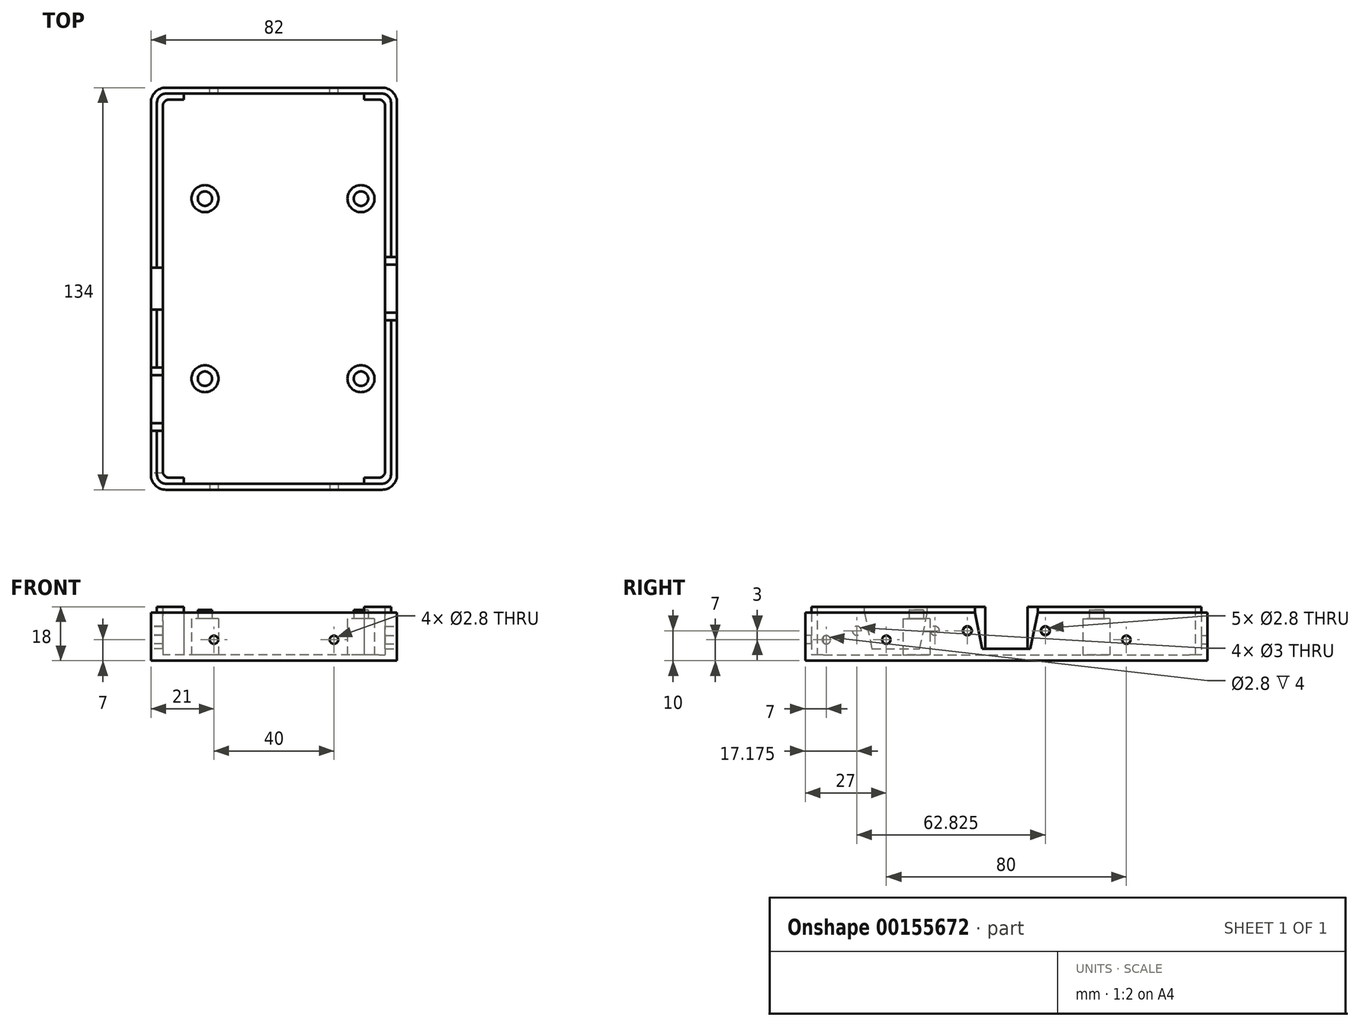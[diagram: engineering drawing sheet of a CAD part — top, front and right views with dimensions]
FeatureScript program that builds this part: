
annotation { "Feature Type Name" : "Feature", "Feature Type Description" : "" }
export const myFeature = defineFeature(function(context is Context, id is Id, definition is map)
    precondition{}
    {
        {
            var Q0;
            Q0=qCreatedBy(makeId("Top.planeOp"),FACE);
            var sketch = newSketch(context, id + "F0", { "sketchPlane" : qUnion([Q0])});
            skLineSegment(sketch, "E0.bottom", {"start": v(36, -67) * mm, "end": v(-36, -67) * mm});
            skLineSegment(sketch, "E0.top", {"start": v(36, 67) * mm, "end": v(-36, 67) * mm});
            skLineSegment(sketch, "E0.left", {"start": v(41, -62) * mm, "end": v(41, 62) * mm});
            skLineSegment(sketch, "E0.right", {"start": v(-41, -62) * mm, "end": v(-41, 62) * mm});
            skPoint(sketch, "E0.middle", {"position": v(0, 0) * mm});
            skPoint(sketch, "E1.visualSharp", {"position": v(-41, 67) * mm});
            skArc(sketch, "E1.filletArc", {"start": v(-36, 67) * mm, "mid": v(-39.54, 65.54) * mm, "end": v(-41, 62) * mm});
            skPoint(sketch, "E2.visualSharp", {"position": v(41, 67) * mm});
            skArc(sketch, "E2.filletArc", {"start": v(41, 62) * mm, "mid": v(39.54, 65.54) * mm, "end": v(36, 67) * mm});
            skPoint(sketch, "E3.visualSharp", {"position": v(41, -67) * mm});
            skArc(sketch, "E3.filletArc", {"start": v(36, -67) * mm, "mid": v(39.54, -65.54) * mm, "end": v(41, -62) * mm});
            skPoint(sketch, "E4.visualSharp", {"position": v(-41, -67) * mm});
            skArc(sketch, "E4.filletArc", {"start": v(-41, -62) * mm, "mid": v(-39.54, -65.54) * mm, "end": v(-36, -67) * mm});
            skSolve(sketch);
        }
        {
            var Q0;
            Q0=qSketchRegion(id+"F0",true);
            extrude(context, id + "F1", {"entities" : qUnion([Q0]), "depth" : 16 * mm});
        }
        {
            var Q0;
            Q0=makeQuery(id+"F1.opExtrude","CAP_FACE",FACE,{"disambiguationData":[OSD([sQuery(id+"F0.wireOp",EDGE,"E0.bottom"),sQuery(id+"F0.wireOp",EDGE,"E0.top"),sQuery(id+"F0.wireOp",EDGE,"E0.left"),sQuery(id+"F0.wireOp",EDGE,"E0.right"),sQuery(id+"F0.wireOp",EDGE,"E1.filletArc"),sQuery(id+"F0.wireOp",EDGE,"E2.filletArc"),sQuery(id+"F0.wireOp",EDGE,"E3.filletArc"),sQuery(id+"F0.wireOp",EDGE,"E4.filletArc")])],"isStart":false});
            shell(context, id + "F2", {"entities" : qUnion([Q0]), "thickness" : 2 * mm});
        }
        {
            var Q0;
            Q0=makeQuery(id+"F2.opShell","OFFSET_FACE",FACE,{"disambiguationData":[OSD([sQuery(id+"F0.wireOp",EDGE,"E0.bottom"),sQuery(id+"F0.wireOp",EDGE,"E0.top"),sQuery(id+"F0.wireOp",EDGE,"E0.left"),sQuery(id+"F0.wireOp",EDGE,"E0.right"),sQuery(id+"F0.wireOp",EDGE,"E1.filletArc"),sQuery(id+"F0.wireOp",EDGE,"E2.filletArc"),sQuery(id+"F0.wireOp",EDGE,"E3.filletArc"),sQuery(id+"F0.wireOp",EDGE,"E4.filletArc")])]});
            var sketch = newSketch(context, id + "F3", { "sketchPlane" : qUnion([Q0])});
            skCircle(sketch, "E5", {"center": v(-23, 30) * mm, "radius": 4.5 * mm});
            skCircle(sketch, "E6", {"center": v(29, 30) * mm, "radius": 4.5 * mm});
            skCircle(sketch, "E7", {"center": v(-23, -30) * mm, "radius": 4.5 * mm});
            skCircle(sketch, "E8", {"center": v(29, -30) * mm, "radius": 4.5 * mm});
            skLineSegment(sketch, "E9.bottom", {"start": v(36, -65) * mm, "end": v(30, -65) * mm});
            skLineSegment(sketch, "E9.top", {"start": v(36, 65) * mm, "end": v(30, 65) * mm});
            skLineSegment(sketch, "E9.left", {"start": v(39, -62) * mm, "end": v(39, 62) * mm});
            skLineSegment(sketch, "E9.right", {"start": v(-39, -62) * mm, "end": v(-39, 62) * mm});
            skPoint(sketch, "E9.middle", {"position": v(0, 0) * mm});
            skLineSegment(sketch, "E10.bottom", {"start": v(35, -63) * mm, "end": v(30, -63) * mm});
            skLineSegment(sketch, "E10.top", {"start": v(35, 63) * mm, "end": v(30, 63) * mm});
            skLineSegment(sketch, "E10.left", {"start": v(37, -61) * mm, "end": v(37, 61) * mm});
            skLineSegment(sketch, "E10.right", {"start": v(-37, -61) * mm, "end": v(-37, 61) * mm});
            skPoint(sketch, "E11.visualSharp", {"position": v(-39, -65) * mm});
            skArc(sketch, "E11.filletArc", {"start": v(-39, -62) * mm, "mid": v(-38.12, -64.12) * mm, "end": v(-36, -65) * mm});
            skPoint(sketch, "E12.visualSharp", {"position": v(39, -65) * mm});
            skArc(sketch, "E12.filletArc", {"start": v(36, -65) * mm, "mid": v(38.12, -64.12) * mm, "end": v(39, -62) * mm});
            skPoint(sketch, "E13.visualSharp", {"position": v(-39, 65) * mm});
            skArc(sketch, "E13.filletArc", {"start": v(-36, 65) * mm, "mid": v(-38.12, 64.12) * mm, "end": v(-39, 62) * mm});
            skPoint(sketch, "E14.visualSharp", {"position": v(39, 65) * mm});
            skArc(sketch, "E14.filletArc", {"start": v(39, 62) * mm, "mid": v(38.12, 64.12) * mm, "end": v(36, 65) * mm});
            skPoint(sketch, "E15.visualSharp", {"position": v(-37, 63) * mm});
            skArc(sketch, "E15.filletArc", {"start": v(-35, 63) * mm, "mid": v(-36.41, 62.41) * mm, "end": v(-37, 61) * mm});
            skPoint(sketch, "E16.visualSharp", {"position": v(37, 63) * mm});
            skArc(sketch, "E16.filletArc", {"start": v(37, 61) * mm, "mid": v(36.41, 62.41) * mm, "end": v(35, 63) * mm});
            skPoint(sketch, "E17.visualSharp", {"position": v(-37, -63) * mm});
            skArc(sketch, "E17.filletArc", {"start": v(-37, -61) * mm, "mid": v(-36.41, -62.41) * mm, "end": v(-35, -63) * mm});
            skPoint(sketch, "E18.visualSharp", {"position": v(37, -63) * mm});
            skArc(sketch, "E18.filletArc", {"start": v(35, -63) * mm, "mid": v(36.41, -62.41) * mm, "end": v(37, -61) * mm});
            skLineSegment(sketch, "E19", {"start": v(-30, 65) * mm, "end": v(-30, 63) * mm});
            skLineSegment(sketch, "E20", {"start": v(30, 65) * mm, "end": v(30, 63) * mm});
            skLineSegment(sketch, "E21.trimOffspring", {"start": v(-30, 65) * mm, "end": v(-36, 65) * mm});
            skLineSegment(sketch, "E22.trimOffspring", {"start": v(-30, 63) * mm, "end": v(-35, 63) * mm});
            skLineSegment(sketch, "E23.trimOffspring", {"start": v(-30, -63) * mm, "end": v(-35, -63) * mm});
            skLineSegment(sketch, "E24.trimOffspring", {"start": v(-30, -65) * mm, "end": v(-36, -65) * mm});
            skLineSegment(sketch, "E25.trimOffspring", {"start": v(30, -63) * mm, "end": v(30, -65) * mm});
            skLineSegment(sketch, "E26.trimOffspring", {"start": v(-30, -63) * mm, "end": v(-30, -65) * mm});
            skSolve(sketch);
        }
        {
            var Q0;
            Q0=makeQuery(id+"F3.imprint","IMPRINT",FACE,{"disambiguationData":[TD([[makeQuery(id+"F3.imprint","IMPRINT",EDGE,{"derivedFrom":sQuery(id+"F3.wireOp",EDGE,"E5")}),1.0]])]});
            var Q1;
            Q1=makeQuery(id+"F3.imprint","IMPRINT",FACE,{"disambiguationData":[TD([[makeQuery(id+"F3.imprint","IMPRINT",EDGE,{"derivedFrom":sQuery(id+"F3.wireOp",EDGE,"E7")}),1.0]])]});
            var Q2;
            Q2=makeQuery(id+"F3.imprint","IMPRINT",FACE,{"disambiguationData":[TD([[makeQuery(id+"F3.imprint","IMPRINT",EDGE,{"derivedFrom":sQuery(id+"F3.wireOp",EDGE,"E8")}),1.0]])]});
            var Q3;
            Q3=makeQuery(id+"F3.imprint","IMPRINT",FACE,{"disambiguationData":[TD([[makeQuery(id+"F3.imprint","IMPRINT",EDGE,{"derivedFrom":sQuery(id+"F3.wireOp",EDGE,"E6")}),1.0]])]});
            extrude(context, id + "F4", {"entities" : qUnion([Q0, Q1, Q2, Q3]), "operationType" : NewBodyOperationType.ADD, "depth" : 12 * mm});
        }
        {
            var Q0;
            Q0=makeQuery(id+"F4.opExtrude","CAP_FACE",FACE,{"disambiguationData":[OSD([sQuery(id+"F3.wireOp",EDGE,"E5")])],"isStart":false});
            var Q1;
            Q1=makeQuery(id+"F4.opExtrude","CAP_FACE",FACE,{"disambiguationData":[OSD([sQuery(id+"F3.wireOp",EDGE,"E6")])],"isStart":false});
            cPlane(context, id + "F5", {"entities" : qUnion([Q0, Q1]), "cplaneType" : CPlaneType.MID_PLANE, "offset" : 25 * mm, "width" : 150 * mm, "height" : 150 * mm});
        }
        {
            var Q0;
            Q0=qCreatedBy(id+"F5.planeOp",FACE);
            var sketch = newSketch(context, id + "F6", { "sketchPlane" : qUnion([Q0])});
            skCircle(sketch, "E27", {"center": v(-23, 30) * mm, "radius": 2.4 * mm});
            skCircle(sketch, "E28", {"center": v(29, 30) * mm, "radius": 2.4 * mm});
            skCircle(sketch, "E29", {"center": v(-23, -30) * mm, "radius": 2.4 * mm});
            skCircle(sketch, "E30", {"center": v(29, -30) * mm, "radius": 2.4 * mm});
            skSolve(sketch);
        }
        {
            var Q0;
            Q0=qSketchRegion(id+"F6",true);
            extrude(context, id + "F7", {"entities" : qUnion([Q0]), "operationType" : NewBodyOperationType.ADD, "depth" : 3 * mm});
        }
        {
            var Q0;
            Q0=makeQuery(id+"F3.imprint","IMPRINT",FACE,{"disambiguationData":[TD([[makeQuery(id+"F3.imprint","IMPRINT",EDGE,{"derivedFrom":sQuery(id+"F3.wireOp",EDGE,"E9.bottom")}),-1.0]])]});
            var Q1;
            Q1=makeQuery(id+"F3.imprint","IMPRINT",FACE,{"disambiguationData":[TD([[makeQuery(id+"F3.imprint","IMPRINT",EDGE,{"derivedFrom":sQuery(id+"F3.wireOp",EDGE,"E9.right")}),-1.0]])]});
            extrude(context, id + "F8", {"entities" : qUnion([Q0, Q1]), "operationType" : NewBodyOperationType.ADD, "depth" : 16 * mm});
        }
        {
            var Q0;
            Q0=makeQuery(id+"F1.opExtrude","SWEPT_FACE",FACE,{"disambiguationData":[OSD([sQuery(id+"F0.wireOp",EDGE,"E0.right")])]});
            var sketch = newSketch(context, id + "F9", { "sketchPlane" : qUnion([Q0])});
            skCircle(sketch, "E31", {"center": v(-13, 10) * mm, "radius": 1.4 * mm});
            skCircle(sketch, "E32", {"center": v(13, 10) * mm, "radius": 1.4 * mm});
            skLineSegment(sketch, "E33.bottom", {"start": v(7, 4) * mm, "end": v(-7, 4) * mm});
            skLineSegment(sketch, "E33.top", {"start": v(7, 16) * mm, "end": v(-7, 16) * mm});
            skLineSegment(sketch, "E33.left", {"start": v(7, 4) * mm, "end": v(7, 16) * mm});
            skLineSegment(sketch, "E33.right", {"start": v(-7, 4) * mm, "end": v(-7, 16) * mm});
            skPoint(sketch, "E33.middle", {"position": v(0, 10) * mm});
            skCircle(sketch, "E34", {"center": v(23.83, 10) * mm, "radius": 1.5 * mm});
            skCircle(sketch, "E35", {"center": v(49.83, 10) * mm, "radius": 1.5 * mm});
            skLineSegment(sketch, "E36", {"start": v(26.33, 16) * mm, "end": v(47.33, 16) * mm});
            skLineSegment(sketch, "E37", {"start": v(47.33, 16) * mm, "end": v(44.83, 4) * mm});
            skLineSegment(sketch, "E38", {"start": v(44.83, 4) * mm, "end": v(28.83, 4) * mm});
            skLineSegment(sketch, "E39", {"start": v(28.83, 4) * mm, "end": v(26.33, 16) * mm});
            skLineSegment(sketch, "E40.bottom", {"start": v(-7, 16) * mm, "end": v(7, 16) * mm});
            skLineSegment(sketch, "E40.top", {"start": v(-7, 18) * mm, "end": v(7, 18) * mm});
            skLineSegment(sketch, "E40.left", {"start": v(-7, 16) * mm, "end": v(-7, 18) * mm});
            skLineSegment(sketch, "E40.right", {"start": v(7, 16) * mm, "end": v(7, 18) * mm});
            skLineSegment(sketch, "E41.top", {"start": v(26.33, 18) * mm, "end": v(47.33, 18) * mm});
            skLineSegment(sketch, "E41.left", {"start": v(26.33, 16) * mm, "end": v(26.33, 18) * mm});
            skLineSegment(sketch, "E41.right", {"start": v(47.33, 16) * mm, "end": v(47.33, 18) * mm});
            skCircle(sketch, "E42", {"center": v(-40, 7) * mm, "radius": 1.4 * mm});
            skCircle(sketch, "E43", {"center": v(60, 7) * mm, "radius": 1.4 * mm});
            skSolve(sketch);
        }
        {
            var Q0;
            Q0=makeQuery(id+"F1.opExtrude","SWEPT_FACE",FACE,{"disambiguationData":[OSD([sQuery(id+"F0.wireOp",EDGE,"E0.left")])]});
            var sketch = newSketch(context, id + "F10", { "sketchPlane" : qUnion([Q0])});
            skCircle(sketch, "E44", {"center": v(-13, 10) * mm, "radius": 1.5 * mm});
            skCircle(sketch, "E45", {"center": v(13, 10) * mm, "radius": 1.5 * mm});
            skLineSegment(sketch, "E46", {"start": v(-10.5, 16) * mm, "end": v(10.5, 16) * mm});
            skLineSegment(sketch, "E47", {"start": v(10.5, 16) * mm, "end": v(8, 4) * mm});
            skLineSegment(sketch, "E48", {"start": v(8, 4) * mm, "end": v(-8, 4) * mm});
            skLineSegment(sketch, "E49", {"start": v(-8, 4) * mm, "end": v(-10.5, 16) * mm});
            skLineSegment(sketch, "E50.top", {"start": v(-10.5, 18) * mm, "end": v(10.5, 18) * mm});
            skLineSegment(sketch, "E50.left", {"start": v(-10.5, 16) * mm, "end": v(-10.5, 18) * mm});
            skLineSegment(sketch, "E50.right", {"start": v(10.5, 16) * mm, "end": v(10.5, 18) * mm});
            skCircle(sketch, "E51", {"center": v(40, 7) * mm, "radius": 1.4 * mm});
            skCircle(sketch, "E52", {"center": v(-40, 7) * mm, "radius": 1.4 * mm});
            skSolve(sketch);
        }
        {
            var Q0;
            Q0=qSketchRegion(id+"F9",true);
            extrude(context, id + "F11", {"entities" : qUnion([Q0]), "operationType" : NewBodyOperationType.REMOVE, "oppositeDirection" : true, "depth" : 4 * mm});
        }
        {
            var Q0;
            Q0=qSketchRegion(id+"F10",true);
            extrude(context, id + "F12", {"entities" : qUnion([Q0]), "operationType" : NewBodyOperationType.REMOVE, "oppositeDirection" : true, "depth" : 4 * mm});
        }
        {
            var Q0;
            Q0=makeQuery(id+"F1.opExtrude","SWEPT_FACE",FACE,{"disambiguationData":[OSD([sQuery(id+"F0.wireOp",EDGE,"E0.top")])]});
            var sketch = newSketch(context, id + "F13", { "sketchPlane" : qUnion([Q0])});
            skCircle(sketch, "E53", {"center": v(20, 7) * mm, "radius": 1.4 * mm});
            skCircle(sketch, "E54", {"center": v(-20, 7) * mm, "radius": 1.4 * mm});
            skSolve(sketch);
        }
        {
            var Q0;
            Q0 = qSketchRegion(id + "F13", true);
            extrude(context, id + "F14", {"entities" : qUnion([Q0]), "operationType" : NewBodyOperationType.REMOVE, "oppositeDirection" : true, "depth" : 2 * mm});
        }
        {
            var Q0;
            Q0=makeQuery(id+"F1.opExtrude","SWEPT_FACE",FACE,{"disambiguationData":[OSD([sQuery(id+"F0.wireOp",EDGE,"E0.bottom")])]});
            var sketch = newSketch(context, id + "F15", { "sketchPlane" : qUnion([Q0])});
            skCircle(sketch, "E55", {"center": v(-20, 7) * mm, "radius": 1.4 * mm});
            skCircle(sketch, "E56", {"center": v(20, 7) * mm, "radius": 1.4 * mm});
            skSolve(sketch);
        }
        {
            var Q0;
            Q0 = qSketchRegion(id + "F15", true);
            extrude(context, id + "F16", {"entities" : qUnion([Q0]), "operationType" : NewBodyOperationType.REMOVE, "oppositeDirection" : true, "depth" : 2 * mm});
        }
    });
